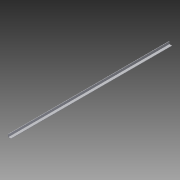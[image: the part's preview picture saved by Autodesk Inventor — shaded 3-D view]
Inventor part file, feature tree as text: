
AUTODESK INVENTOR PART (.ipt)
format: ipt  version: 2014 SP1 (Build 180222100, 222)  size: 75,264 bytes
history: native  units: in
note: dims shown in document units (in); Inventor stores cm internally (conversion verified against a paired STEP export)
features: extrude x1, sketch x1
ambient origin geometry x8: Origin, YZ Plane, XZ Plane, XY Plane, X Axis, Y Axis, Z Axis, Center Point
bodies: Solid1 (feature_tree)
feature tree (2):
  extrude  "Extrusion1"  Depth=0.0625in
  sketch  "Sketch1"  dims[d0=0.5in d1=0.0625in d2=0.5in d3=0.0625in d4=28.375in d5=0.0in]
